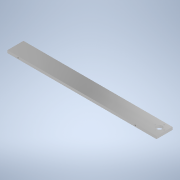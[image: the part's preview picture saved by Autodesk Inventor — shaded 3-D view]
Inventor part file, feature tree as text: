
AUTODESK INVENTOR PART (.ipt)
format: ipt  version: 2022 (Build 260153000, 153)  size: 140,800 bytes
history: native  units: mm
features: sketch x4, hole x3, other x1, extrude x1
ambient origin geometry x8: Origin, YZ Plane, XZ Plane, XY Plane, X Axis, Y Axis, Z Axis, Center Point
bodies: Body1 (feature_tree)
feature tree (9):
  other  "ソリッド1"
  extrude  "押し出し1"  Depth=30.0mm
  hole  "穴1"  [1 undecoded]
  hole  "穴3"  [1 undecoded]
  hole  "穴4"  [1 undecoded]
  sketch  "スケッチ1"
  sketch  "スケッチ2"
  sketch  "スケッチ4"
  sketch  "スケッチ5"
note: 3 required parameter values undecoded (feature->parameter linkage not recoverable at this tier; creation-order binding heuristic only, values carry confidence <= 0.55)
